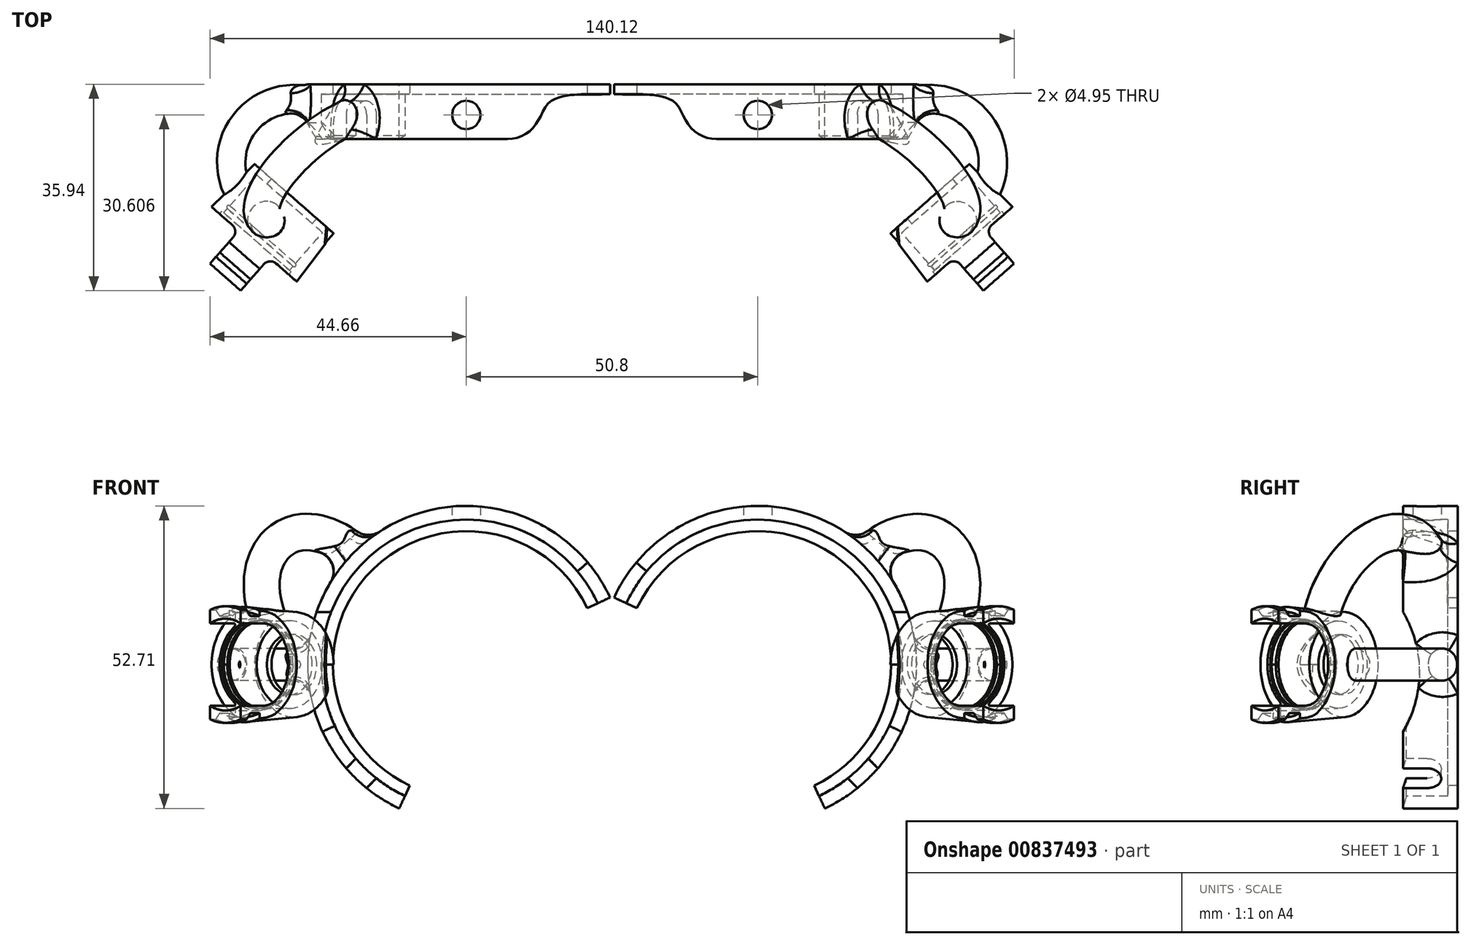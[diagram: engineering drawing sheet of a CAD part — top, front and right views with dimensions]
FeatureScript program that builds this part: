
annotation { "Feature Type Name" : "Feature", "Feature Type Description" : "" }
export const myFeature = defineFeature(function(context is Context, id is Id, definition is map)
    precondition{}
    {
        {
            var Q0;
            Q0=qCreatedBy(makeId("Front.planeOp"),FACE);
            var sketch = newSketch(context, id + "F0", { "sketchPlane" : qUnion([Q0])});
            skCircle(sketch, "E0", {"center": v(0, 0) * mm, "radius": 25.27 * mm, "construction": true});
            skCircle(sketch, "E1", {"center": v(0, 0) * mm, "radius": 23.24 * mm, "construction": true});
            skLineSegment(sketch, "E2", {"start": v(0, 0) * mm, "end": v(0, 25.27) * mm, "construction": true});
            skLineSegment(sketch, "E3", {"start": v(0, 0) * mm, "end": v(25.27, 0) * mm, "construction": true});
            skLineSegment(sketch, "E4", {"start": v(0, 0) * mm, "end": v(17.87, 17.87) * mm, "construction": true});
            skCircle(sketch, "E5", {"center": v(0, 0) * mm, "radius": 15.88 * mm, "construction": true});
            skPoint(sketch, "E6", {"position": v(17.87, 17.86) * mm});
            skLineSegment(sketch, "E7", {"start": v(0, 0) * mm, "end": v(17.55, -18.17) * mm, "construction": true});
            skPoint(sketch, "E8", {"position": v(17.88, -17.85) * mm});
            skSolve(sketch);
        }
        {
            var Q0;
            Q0=qCreatedBy(makeId("Right.planeOp"),FACE);
            var sketch = newSketch(context, id + "F1", { "sketchPlane" : qUnion([Q0])});
            skLineSegment(sketch, "E9.0", {"start": v(0, -25.27) * mm, "end": v(0, 25.27) * mm, "construction": true});
            skLineSegment(sketch, "E9.1", {"start": v(0, -23.24) * mm, "end": v(0, 23.24) * mm, "construction": true});
            skLineSegment(sketch, "E10", {"start": v(0, 23.24) * mm, "end": v(-1.73, 23.24) * mm});
            skLineSegment(sketch, "E11", {"start": v(-1.73, 23.24) * mm, "end": v(-1.73, 25.27) * mm});
            skLineSegment(sketch, "E12", {"start": v(-1.73, 25.27) * mm, "end": v(-9.53, 25.27) * mm});
            skLineSegment(sketch, "E13", {"start": v(0, 23.24) * mm, "end": v(0, 25.27) * mm});
            skLineSegment(sketch, "E14", {"start": v(-9.53, 25.27) * mm, "end": v(-9.53, 27.65) * mm});
            skLineSegment(sketch, "E15", {"start": v(-9.53, 27.65) * mm, "end": v(0, 27.65) * mm});
            skLineSegment(sketch, "E16", {"start": v(0, 27.65) * mm, "end": v(0, 25.27) * mm});
            skLineSegment(sketch, "E17", {"start": v(0, 0) * mm, "end": v(1.7, 0) * mm, "construction": true});
            skLineSegment(sketch, "E18.0", {"start": v(0, -15.88) * mm, "end": v(0, 15.88) * mm, "construction": true});
            skLineSegment(sketch, "E19", {"start": v(0, 15.88) * mm, "end": v(14.29, 15.88) * mm, "construction": true});
            skLineSegment(sketch, "E20", {"start": v(0, -15.88) * mm, "end": v(14.29, -15.88) * mm, "construction": true});
            skLineSegment(sketch, "E21", {"start": v(0, 27.65) * mm, "end": v(-14.29, 27.65) * mm, "construction": true});
            skLineSegment(sketch, "E22", {"start": v(0, -25.27) * mm, "end": v(-14.29, -25.27) * mm, "construction": true});
            skLineSegment(sketch, "E23", {"start": v(14.29, 15.88) * mm, "end": v(14.29, -15.88) * mm, "construction": true});
            skLineSegment(sketch, "E24", {"start": v(14.29, 0) * mm, "end": v(26.99, 0) * mm});
            skPoint(sketch, "E25", {"position": v(-5.16, 27.65) * mm});
            skSolve(sketch);
        }
        {
            var Q0;
            Q0=makeQuery(id+"F1.imprint","IMPRINT",FACE,{"disambiguationData":[TD([[makeQuery(id+"F1.imprint","IMPRINT",EDGE,{"derivedFrom":sQuery(id+"F1.wireOp",EDGE,"E10")}),-1.0]])]});
            var Q1;
            Q1=sQuery(id+"F1.wireOp",EDGE,"E17");
            revolve(context, id + "F2", {"surfaceOperationType" : NewSurfaceOperationType.NEW, "entities" : qUnion([Q0]), "axis" : qUnion([Q1]), "revolveType" : RevolveType.TWO_DIRECTIONS, "angle" : 115 * degree, "angleBack" : 310 * degree});
        }
        {
            var Q0;
            Q0=qCreatedBy(makeId("Top.planeOp"),FACE);
            var sketch = newSketch(context, id + "F3", { "sketchPlane" : qUnion([Q0])});
            skLineSegment(sketch, "E26.0", {"start": v(0, 14.29) * mm, "end": v(0, 26.99) * mm});
            skLineSegment(sketch, "E26.1.0", {"start": v(-21.18, -9.53) * mm, "end": v(27.65, -9.53) * mm});
            skLineSegment(sketch, "E26.1.1", {"start": v(25.06, -9.53) * mm, "end": v(25.06, 0) * mm});
            skLineSegment(sketch, "E26.1.2", {"start": v(27.65, 0) * mm, "end": v(-21.18, 0) * mm});
            skLineSegment(sketch, "E26.1.3", {"start": v(-21.18, 0) * mm, "end": v(-21.18, -9.53) * mm});
            skLineSegment(sketch, "E27", {"start": v(0, 14.29) * mm, "end": v(5.73, 19.31) * mm, "construction": true});
            skLineSegment(sketch, "E28", {"start": v(0, 14.29) * mm, "end": v(25.06, -14.29) * mm, "construction": true});
            skLineSegment(sketch, "E29", {"start": v(5.73, 19.31) * mm, "end": v(36.52, -15.8) * mm, "construction": true});
            skLineSegment(sketch, "E30", {"start": v(25.06, -9.53) * mm, "end": v(25.06, -19.05) * mm, "construction": true});
            skLineSegment(sketch, "E31.MirrorCS", {"start": v(-5.73, 9.26) * mm, "end": v(25.06, -25.85) * mm, "construction": true});
            skLineSegment(sketch, "E32.MirrorCS", {"start": v(0, 14.29) * mm, "end": v(-5.73, 9.26) * mm, "construction": true});
            skLineSegment(sketch, "E33", {"start": v(25.06, -19.05) * mm, "end": v(25.06, -25.85) * mm});
            skLineSegment(sketch, "E34", {"start": v(25.06, -25.85) * mm, "end": v(36.52, -15.8) * mm, "construction": true});
            skLineSegment(sketch, "E35", {"start": v(36.52, -15.8) * mm, "end": v(34.72, -17.37) * mm});
            skLineSegment(sketch, "E36", {"start": v(34.72, -17.37) * mm, "end": v(33.94, -16.47) * mm});
            skLineSegment(sketch, "E37", {"start": v(36.52, -15.8) * mm, "end": v(42.27, -22.36) * mm});
            skLineSegment(sketch, "E38", {"start": v(42.27, -22.36) * mm, "end": v(43.42, -21.36) * mm});
            skLineSegment(sketch, "E39", {"start": v(43.42, -21.36) * mm, "end": v(36.88, -13.9) * mm});
            skLineSegment(sketch, "E40", {"start": v(33.94, -16.47) * mm, "end": v(36.88, -13.9) * mm});
            skLineSegment(sketch, "E41", {"start": v(42.56, -22.11) * mm, "end": v(48, -28.32) * mm});
            skLineSegment(sketch, "E42", {"start": v(43.42, -21.36) * mm, "end": v(48.86, -27.56) * mm});
            skLineSegment(sketch, "E43", {"start": v(48, -28.32) * mm, "end": v(48.86, -27.56) * mm});
            skLineSegment(sketch, "E44", {"start": v(30.79, -20.82) * mm, "end": v(32.6, -22.88) * mm, "construction": true});
            skLineSegment(sketch, "E45", {"start": v(48.86, -27.56) * mm, "end": v(49.62, -26.9) * mm});
            skLineSegment(sketch, "E46", {"start": v(49.62, -26.9) * mm, "end": v(48.58, -25.7) * mm});
            skLineSegment(sketch, "E47", {"start": v(48.58, -25.7) * mm, "end": v(47.81, -26.37) * mm});
            skLineSegment(sketch, "E48", {"start": v(36.32, -15.96) * mm, "end": v(42.27, -22.36) * mm});
            skLineSegment(sketch, "E49", {"start": v(45.55, -23.8) * mm, "end": v(46.22, -23.2) * mm});
            skLineSegment(sketch, "E50", {"start": v(46.22, -23.2) * mm, "end": v(36.88, -13.9) * mm});
            skCircle(sketch, "E51", {"center": v(41.43, -21.4) * mm, "radius": 0.32 * mm});
            skSolve(sketch);
        }
        {
            var Q0;
            Q0=makeQuery(id+"F3.imprint","IMPRINT",FACE,{"disambiguationData":[TD([[makeQuery(id+"F3.imprint","IMPRINT",EDGE,{"derivedFrom":sQuery(id+"F3.wireOp",EDGE,"E35")}),-1.0]])]});
            var Q1;
            {var subQ2=sQuery(id+"F3.wireOp",EDGE,"E41");Q1=makeQuery(id+"F3.imprint","IMPRINT",FACE,{"disambiguationData":[TD([[makeQuery(id+"F3.imprint","IMPRINT",EDGE,{"derivedFrom":subQ2}),1.0]])]});}
            var Q2;
            {var subQ0=sQuery(id+"F3.wireOp",EDGE,"E45");Q2=makeQuery(id+"F3.imprint","IMPRINT",FACE,{"disambiguationData":[TD([[makeQuery(id+"F3.imprint","IMPRINT",EDGE,{"derivedFrom":subQ0}),1.0]])]});}
            var Q3;
            {var subQ0=sQuery(id+"F3.wireOp",EDGE,"ZS8Crhrf-CrOi-06I2-Trp5-8wOd5zCYoBhE");Q3=makeQuery(id+"F3.imprint","IMPRINT",FACE,{"disambiguationData":[TD([[makeQuery(id+"F3.imprint","IMPRINT",EDGE,{"derivedFrom":subQ0}),-1.0]])]});}
            var Q4;
            {var subQ0=sQuery(id+"F3.wireOp",EDGE,"E39");Q4=makeQuery(id+"F3.imprint","IMPRINT",FACE,{"disambiguationData":[TD([[makeQuery(id+"F3.imprint","IMPRINT",EDGE,{"derivedFrom":subQ0}),-1.0]])]});}
            var Q5;
            {var subQ0=sQuery(id+"F3.wireOp",EDGE,"E51");var subQ1=sQuery(id+"F3.wireOp",EDGE,"E37");var subQ2=makeQuery(id+"F3.imprint","INTERSECT",VERTEX,{"disambiguationData":[OD(0.0)],"derivedFrom":[subQ1,subQ0]});Q5=makeQuery(id+"F3.imprint","IMPRINT",FACE,{"disambiguationData":[TD([[makeQuery(id+"F3.imprint","IMPRINT",EDGE,{"disambiguationData":[TD([[subQ2,-1.0]])],"derivedFrom":subQ1}),1.0]])]});}
            var Q6;
            Q6=sQuery(id+"F3.wireOp",EDGE,"E44");
            var Q7;
            Q7=sQuery(id+"F3.wireOp",EDGE,"E44");
            revolve(context, id + "F4", {"operationType" : NewBodyOperationType.ADD, "surfaceOperationType" : NewSurfaceOperationType.NEW, "entities" : qUnion([Q0, Q1, Q2, Q3, Q4, Q5]), "surfaceEntities" : qUnion([Q6]), "axis" : qUnion([Q7]), "revolveType" : RevolveType.FULL});
        }
        {
            var Q0;
            Q0=qCreatedBy(makeId("Right.planeOp"),FACE);
            var sketch = newSketch(context, id + "F5", { "sketchPlane" : qUnion([Q0])});
            skEllipse(sketch, "E52.0", {"center": v(-19.93, 0) * mm, "majorRadius": 8.76 * mm, "minorRadius": 5.18 * mm, "majorAxis": v(0, -1), "construction": true});
            skLineSegment(sketch, "E52.1.0", {"start": v(-9.53, 27.65) * mm, "end": v(-9.53, -11.68) * mm, "construction": true});
            skLineSegment(sketch, "E52.1.1", {"start": v(-9.53, -11.68) * mm, "end": v(0, -11.68) * mm});
            skLineSegment(sketch, "E52.1.2", {"start": v(0, -11.68) * mm, "end": v(0, 27.65) * mm});
            skLineSegment(sketch, "E52.1.3", {"start": v(0, 17.77) * mm, "end": v(-9.53, 17.77) * mm, "construction": true});
            skLineSegment(sketch, "E53", {"start": v(-19.93, 0) * mm, "end": v(-9.53, 0) * mm, "construction": true});
            skLineSegment(sketch, "E54", {"start": v(-19.93, 9.14) * mm, "end": v(-9.53, 9.14) * mm, "construction": true});
            skLineSegment(sketch, "E55", {"start": v(-19.93, -9.14) * mm, "end": v(-9.53, -9.14) * mm, "construction": true});
            skLineSegment(sketch, "E56", {"start": v(-9.53, 9.14) * mm, "end": v(-9.53, -9.14) * mm});
            skArc(sketch, "E57", {"start": v(-9.53, -11.68) * mm, "mid": v(-6.65, -1.27) * mm, "end": v(-9.53, 9.14) * mm});
            skLineSegment(sketch, "E58", {"start": v(-9.53, -9.14) * mm, "end": v(-9.53, -11.68) * mm});
            skSolve(sketch);
        }
        {
            var Q0;
            Q0=makeQuery(id+"F5.imprint","IMPRINT",FACE,{"disambiguationData":[TD([[makeQuery(id+"F5.imprint","IMPRINT",EDGE,{"derivedFrom":sQuery(id+"F5.wireOp",EDGE,"GxEW9ax0-zjAY-ybk5-duMN-0JDvZg63hfbD")}),1.0]])]});
            var Q1;
            Q1=makeQuery(id+"F5.imprint","IMPRINT",FACE,{"disambiguationData":[TD([[makeQuery(id+"F5.imprint","IMPRINT",EDGE,{"derivedFrom":sQuery(id+"F5.wireOp",EDGE,"E56")}),1.0]])]});
            extrude(context, id + "F6", {"entities" : qUnion([Q0, Q1]), "operationType" : NewBodyOperationType.REMOVE, "depth" : 50.57 * mm, "offsetDistance" : 25.4 * mm});
        }
        {
            var Q0;
            Q0=qCreatedBy(makeId("Top.planeOp"),FACE);
            var sketch = newSketch(context, id + "F7", { "sketchPlane" : qUnion([Q0])});
            skLineSegment(sketch, "E59.1.0", {"start": v(-21.18, -9.53) * mm, "end": v(26.26, -9.53) * mm, "construction": true});
            skLineSegment(sketch, "E59.1.2", {"start": v(25.06, -11.07) * mm, "end": v(25.06, 0) * mm, "construction": true});
            skLineSegment(sketch, "E59.1.3", {"start": v(27.65, 0) * mm, "end": v(-21.18, 0) * mm, "construction": true});
            skLineSegment(sketch, "E59.1.4", {"start": v(-21.18, 0) * mm, "end": v(-21.18, -9.53) * mm});
            skLineSegment(sketch, "E60.0", {"start": v(26.06, -23.38) * mm, "end": v(33.94, -16.47) * mm, "construction": true});
            skLineSegment(sketch, "E60.1", {"start": v(23.13, -25.95) * mm, "end": v(36.88, -13.9) * mm, "construction": true});
            skLineSegment(sketch, "E60.3", {"start": v(30.81, -32.4) * mm, "end": v(42.27, -22.36) * mm, "construction": true});
            skLineSegment(sketch, "E60.4", {"start": v(25.06, -25.85) * mm, "end": v(36.52, -15.8) * mm, "construction": true});
            skLineSegment(sketch, "E61", {"start": v(36.52, -15.8) * mm, "end": v(42.27, -22.36) * mm, "construction": true});
            skPoint(sketch, "E62", {"position": v(25.06, -3.81) * mm});
            skPoint(sketch, "E62.positionSnap0", {"position": v(27.71, -3.81) * mm});
            skArc(sketch, "E63", {"start": v(39.4, -19.08) * mm, "mid": v(37.93, -6.1) * mm, "end": v(25.06, -3.81) * mm});
            skSolve(sketch);
        }
        {
            var Q0;
            Q0=sQuery(id+"F7.wireOp",EDGE,"E59.1.2");
            cPlane(context, id + "F8", {"entities" : qUnion([Q0]), "cplaneType" : CPlaneType.LINE_ANGLE, "offset" : 25.4 * mm, "angle" : 90 * degree, "width" : 152.4 * mm, "height" : 152.4 * mm});
        }
        {
            var Q0;
            Q0=qCreatedBy(id+"F8.planeOp",FACE);
            var sketch = newSketch(context, id + "F9", { "sketchPlane" : qUnion([Q0])});
            skPoint(sketch, "E64.0", {"position": v(-3.81, 0) * mm});
            skCircle(sketch, "E65", {"center": v(-3.81, 0) * mm, "radius": 2.8 * mm});
            skSolve(sketch);
        }
        {
            var Q0;
            Q0=qSketchRegion(id+"F9",true);
            var Q1;
            Q1=sQuery(id+"F7.wireOp",EDGE,"E63");
            sweep(context, id + "F10", {"operationType" : NewBodyOperationType.ADD, "profiles" : qUnion([Q0]), "path" : qUnion([Q1])});
        }
        {
            var Q0;
            Q0=makeQuery(id+"F2.opRevolve","SWEPT_FACE",FACE,{"disambiguationData":[OSD([sQuery(id+"F1.wireOp",EDGE,"E11")])]});
            var sketch = newSketch(context, id + "F11", { "sketchPlane" : qUnion([Q0])});
            skPoint(sketch, "E66.0", {"position": v(17.87, 17.86) * mm});
            skSolve(sketch);
        }
        {
            var Q0;
            Q0=sQuery(id+"F11.wireOp",VERTEX,"E66.0");
            var Q1;
            Q1=sQuery(id+"F0.wireOp",VERTEX,"E4.end");
            var Q2;
            Q2=sQuery(id+"F0.wireOp",VERTEX,"E6");
            cPlane(context, id + "F12", {"entities" : qUnion([Q0, Q1, Q2]), "cplaneType" : CPlaneType.THREE_POINT, "offset" : 25.4 * mm, "width" : 152.4 * mm, "height" : 152.4 * mm});
        }
        {
            var Q0;
            Q0=makeQuery(id+"F4.opRevolve","SWEPT_FACE",FACE,{"disambiguationData":[OSD([sQuery(id+"F3.wireOp",EDGE,"E35")])]});
            var sketch = newSketch(context, id + "F13", { "sketchPlane" : qUnion([Q0])});
            skPoint(sketch, "E67.0", {"position": v(13.44, 17.86) * mm});
            skLineSegment(sketch, "E68", {"start": v(13.03, 18) * mm, "end": v(8.4, 5.09) * mm, "construction": true});
            skSolve(sketch);
        }
        {
            var Q0;
            Q0=qCreatedBy(id+"F12.planeOp",FACE);
            var sketch = newSketch(context, id + "F14", { "sketchPlane" : qUnion([Q0])});
            skLineSegment(sketch, "E69", {"start": v(0, 0) * mm, "end": v(-9.53, 0) * mm, "construction": true});
            skLineSegment(sketch, "E70.0", {"start": v(-9.53, -5.93) * mm, "end": v(-9.53, 27.65) * mm, "construction": true});
            skCircle(sketch, "E71", {"center": v(-4.76, 0) * mm, "radius": 3.18 * mm});
            skSolve(sketch);
        }
        {
            var Q0;
            Q0=sQuery(id+"F14.wireOp",EDGE,"E69");
            cPoint(context, id + "F15", {"entities" : qUnion([Q0]), "parameter" : 0.5});
        }
        {
            var Q0;
            Q0=sQuery(id+"F13.wireOp",VERTEX,"E68.end");
            var Q1;
            Q1=sQuery(id+"F13.wireOp",VERTEX,"E67.0");
            var Q2;
            Q2=qCreatedBy(id+"F15",VERTEX);
            cPlane(context, id + "F16", {"entities" : qUnion([Q0, Q1, Q2]), "cplaneType" : CPlaneType.THREE_POINT, "offset" : 25.4 * mm, "width" : 152.4 * mm, "height" : 152.4 * mm});
        }
        {
            var Q0;
            Q0=qCreatedBy(id+"F16.planeOp",FACE);
            var sketch = newSketch(context, id + "F17", { "sketchPlane" : qUnion([Q0])});
            skEllipse(sketch, "E72.0", {"center": v(-35.76, -9.46) * mm, "majorRadius": 7.47 * mm, "minorRadius": 0.91 * mm, "majorAxis": v(0.35, -0.94), "construction": true});
            skEllipse(sketch, "E72.1", {"center": v(-43.87, -12.44) * mm, "majorRadius": 7.47 * mm, "minorRadius": 0.91 * mm, "majorAxis": v(0.35, -0.94), "construction": true});
            skLineSegment(sketch, "E73", {"start": v(-38.39, -2.3) * mm, "end": v(-46.5, -5.3) * mm, "construction": true});
            skPoint(sketch, "E74.0", {"position": v(-21.71, 13.75) * mm});
            skArc(sketch, "E75", {"start": v(-21.71, 13.75) * mm, "mid": v(-38.99, 13.14) * mm, "end": v(-42.45, -3.8) * mm});
            skSolve(sketch);
        }
        {
            var Q0;
            Q0=qSketchRegion(id+"F14",true);
            var Q1;
            Q1=sQuery(id+"F17.wireOp",EDGE,"E75");
            sweep(context, id + "F18", {"operationType" : NewBodyOperationType.ADD, "profiles" : qUnion([Q0]), "path" : qUnion([Q1])});
        }
        {
            var Q0;
            Q0=qCreatedBy(makeId("Top.planeOp"),FACE);
            var sketch = newSketch(context, id + "F19", { "sketchPlane" : qUnion([Q0])});
            skLineSegment(sketch, "E76.0", {"start": v(30.53, -32.66) * mm, "end": v(42.56, -22.11) * mm, "construction": true});
            skLineSegment(sketch, "E77.0", {"start": v(22.9, -1.73) * mm, "end": v(22.9, -1.73) * mm});
            skLineSegment(sketch, "E78.0", {"start": v(-21.18, -9.53) * mm, "end": v(-21.18, 0) * mm, "construction": true});
            skLineSegment(sketch, "E78.1", {"start": v(-7.2, -9.53) * mm, "end": v(-21.18, -9.53) * mm, "construction": true});
            skLineSegment(sketch, "E79", {"start": v(-21.18, -1.73) * mm, "end": v(-25.57, -1.73) * mm});
            skLineSegment(sketch, "E80", {"start": v(-25.57, -1.73) * mm, "end": v(-25.57, -14.68) * mm});
            skLineSegment(sketch, "E81", {"start": v(-25.57, -14.68) * mm, "end": v(-7.2, -14.68) * mm});
            skLineSegment(sketch, "E82", {"start": v(-7.2, -14.68) * mm, "end": v(-7.2, -9.53) * mm});
            skFitSpline(sketch, "E83", {"points": [v(42.56, -22.11) * mm, v(35.64, -31.83) * mm, v(34.35, -40.3) * mm], "startDerivative": vector(-16.46, -14.44) * mm, "endDerivative": vector(-39.72, -35.09) * mm, "construction": true});
            skLineSegment(sketch, "E84", {"start": v(42.56, -22.11) * mm, "end": v(44.84, -20.17) * mm});
            skLineSegment(sketch, "E85", {"start": v(44.84, -20.17) * mm, "end": v(52.02, -28.58) * mm});
            skLineSegment(sketch, "E86", {"start": v(52.02, -28.58) * mm, "end": v(36.12, -42.17) * mm});
            skLineSegment(sketch, "E87", {"start": v(36.12, -42.17) * mm, "end": v(34.35, -40.3) * mm});
            skFitSpline(sketch, "E88", {"points": [v(-21.18, -1.73) * mm, v(-12.95, -5.57) * mm, v(-7.2, -9.53) * mm], "startDerivative": vector(39.3, 0) * mm, "endDerivative": vector(20.69, 0) * mm});
            skSolve(sketch);
        }
        {
            var Q0;
            Q0=qSketchRegion(id+"F19",true);
            extrude(context, id + "F20", {"entities" : qUnion([Q0]), "operationType" : NewBodyOperationType.REMOVE, "endBound" : BoundingType.SYMMETRIC, "oppositeDirection" : true, "depth" : 82.8 * mm, "offsetDistance" : 25.4 * mm});
        }
        {
            var Q0;
            Q0=qCreatedBy(makeId("Top.planeOp"),FACE);
            var sketch = newSketch(context, id + "F21", { "sketchPlane" : qUnion([Q0])});
            skCircle(sketch, "E89", {"center": v(0, -5.33) * mm, "radius": 2.48 * mm});
            skSolve(sketch);
        }
        {
            var Q0;
            Q0=makeQuery(id+"F21.imprint","IMPRINT",FACE,{"disambiguationData":[TD([[makeQuery(id+"F21.imprint","IMPRINT",EDGE,{"derivedFrom":sQuery(id+"F21.wireOp",EDGE,"E89")}),1.0]])]});
            extrude(context, id + "F22", {"entities" : qUnion([Q0]), "operationType" : NewBodyOperationType.REMOVE, "depth" : 31.5 * mm, "offsetDistance" : 25.4 * mm});
        }
        {
            var Q0;
            Q0=makeQuery(id+"F10.opSweep","CAP_EDGE",EDGE,{"disambiguationData":[OSD([sQuery(id+"F7.wireOp",VERTEX,"E63.start"),sQuery(id+"F9.wireOp",EDGE,"E65")])],"isStart":false});
            chamfer(context, id + "F23", {"entities" : qUnion([Q0]), "width" : 1.52 * mm, "tangentPropagation" : true});
        }
        {
            var Q0;
            Q0=makeQuery(id+"F2.opRevolve","SWEPT_FACE",FACE,{"disambiguationData":[OSD([sQuery(id+"F1.wireOp",EDGE,"E11")])]});
            var sketch = newSketch(context, id + "F24", { "sketchPlane" : qUnion([Q0])});
            skArc(sketch, "E90.0", {"start": v(22.9, -10.68) * mm, "mid": v(24.44, -6.4) * mm, "end": v(25.2, -1.92) * mm});
            skCircle(sketch, "E91", {"center": v(0, 0) * mm, "radius": 24.48 * mm});
            skArc(sketch, "E92.0", {"start": v(25.2, 1.92) * mm, "mid": v(-25.27, 0) * mm, "end": v(25.2, -1.92) * mm});
            skPoint(sketch, "E93.0", {"position": v(17.87, 17.86) * mm});
            skCircle(sketch, "E94", {"center": v(0, 0) * mm, "radius": 25.27 * mm});
            skSolve(sketch);
        }
        {
            var Q0;
            {var subQ1=sQuery(id+"F1.wireOp",EDGE,"E11");var subQ6=makeQuery(id+"F2.opRevolve","SWEPT_EDGE",EDGE,{"disambiguationData":[OSD([sQuery(id+"F1.wireOp",EDGE,"E10"),subQ1])]});Q0=makeQuery(id+"F24.imprint","IMPRINT",FACE,{"disambiguationData":[TD([[makeQuery(id+"F24.imprint","IMPRINT",EDGE,{"derivedFrom":subQ6}),1.0]])]});}
            var Q1;
            {var subQ1=sQuery(id+"F1.wireOp",EDGE,"E11");var subQ6=makeQuery(id+"F2.opRevolve","SWEPT_EDGE",EDGE,{"disambiguationData":[OSD([sQuery(id+"F1.wireOp",EDGE,"E10"),subQ1])]});Q1=makeQuery(id+"F24.imprint","IMPRINT",FACE,{"disambiguationData":[TD([[makeQuery(id+"F24.imprint","IMPRINT",EDGE,{"derivedFrom":subQ6}),-1.0]])]});}
            extrude(context, id + "F25", {"entities" : qUnion([Q0, Q1]), "operationType" : NewBodyOperationType.REMOVE, "depth" : 43.43 * mm, "offsetDistance" : 25.4 * mm});
        }
        {
            var Q0;
            Q0=makeQuery(id+"F2.opRevolve","CAP_FACE",FACE,{"disambiguationData":[OSD([sQuery(id+"F1.wireOp",EDGE,"E10"),sQuery(id+"F1.wireOp",EDGE,"E11"),sQuery(id+"F1.wireOp",EDGE,"E12"),sQuery(id+"F1.wireOp",EDGE,"E13"),sQuery(id+"F1.wireOp",EDGE,"E14"),sQuery(id+"F1.wireOp",EDGE,"E15"),sQuery(id+"F1.wireOp",EDGE,"E16")])],"isStart":false});
            var Q1;
            Q1=sQuery(id+"F1.wireOp",EDGE,"E24");
            revolve(context, id + "F26", {"operationType" : NewBodyOperationType.ADD, "surfaceOperationType" : NewSurfaceOperationType.NEW, "entities" : qUnion([Q0]), "axis" : qUnion([Q1]), "revolveType" : RevolveType.ONE_DIRECTION, "angle" : 40 * degree});
        }
        {
            var Q0;
            {var subQ0=sQuery(id+"F1.wireOp",EDGE,"E11");Q0=makeQuery(id+"F26.boolean.opBoolean","MERGE",FACE,{"derivedFrom":[makeQuery(id+"F2.opRevolve","SWEPT_FACE",FACE,{"disambiguationData":[OSD([subQ0])]}),makeQuery(id+"F26.opRevolve","SWEPT_FACE",FACE,{"disambiguationData":[OSD([subQ0])]})]});}
            var sketch = newSketch(context, id + "F27", { "sketchPlane" : qUnion([Q0])});
            skPoint(sketch, "E95.0", {"position": v(17.55, -18.17) * mm});
            skSolve(sketch);
        }
        {
            var Q0;
            Q0=sQuery(id+"F0.wireOp",VERTEX,"E7.end");
            var Q1;
            Q1=sQuery(id+"F0.wireOp",VERTEX,"E8");
            var Q2;
            Q2=sQuery(id+"F27.wireOp",VERTEX,"E95.0");
            cPlane(context, id + "F28", {"entities" : qUnion([Q0, Q1, Q2]), "cplaneType" : CPlaneType.THREE_POINT, "offset" : 25.4 * mm, "width" : 152.4 * mm, "height" : 152.4 * mm});
        }
        {
            var Q0;
            Q0=qCreatedBy(id+"F28.planeOp",FACE);
            var sketch = newSketch(context, id + "F29", { "sketchPlane" : qUnion([Q0])});
            skCircle(sketch, "E96", {"center": v(-0.23, -5.33) * mm, "radius": 2.48 * mm});
            skPoint(sketch, "E97.0", {"position": v(-0.23, 0) * mm});
            skLineSegment(sketch, "E98.0", {"start": v(-9.24, -9.52) * mm, "end": v(9.67, -9.52) * mm});
            skLineSegment(sketch, "E99", {"start": v(2.25, -5.33) * mm, "end": v(2.25, -9.52) * mm});
            skLineSegment(sketch, "E100", {"start": v(-2.7, -5.33) * mm, "end": v(-2.7, -9.52) * mm});
            skSolve(sketch);
        }
        {
            var Q0;
            Q0 = qSketchRegion(id + "F29", true);
            extrude(context, id + "F30", {"entities" : qUnion([Q0]), "operationType" : NewBodyOperationType.REMOVE, "endBound" : BoundingType.SYMMETRIC, "oppositeDirection" : true, "depth" : 25.4 * mm, "offsetDistance" : 25.4 * mm});
        }
        {
            var Q0;
            Q0=makeQuery(id+"F2.opRevolve","CAP_FACE",FACE,{"disambiguationData":[OSD([sQuery(id+"F1.wireOp",EDGE,"E10"),sQuery(id+"F1.wireOp",EDGE,"E11"),sQuery(id+"F1.wireOp",EDGE,"E12"),sQuery(id+"F1.wireOp",EDGE,"E13"),sQuery(id+"F1.wireOp",EDGE,"E14"),sQuery(id+"F1.wireOp",EDGE,"E15"),sQuery(id+"F1.wireOp",EDGE,"E16")])],"isStart":true});
            var Q1;
            Q1=sQuery(id+"F1.wireOp",EDGE,"E24");
            revolve(context, id + "F31", {"operationType" : NewBodyOperationType.ADD, "surfaceOperationType" : NewSurfaceOperationType.NEW, "entities" : qUnion([Q0]), "axis" : qUnion([Q1]), "revolveType" : RevolveType.ONE_DIRECTION, "oppositeDirection" : true, "angle" : 15 * degree});
        }
        {
            var Q0;
            Q0=makeQuery(id+"F25.boolean.opBoolean","COPY",FACE,{"derivedFrom":makeQuery(id+"F25.opExtrude","SWEPT_FACE",FACE,{"disambiguationData":[OSD([sQuery(id+"F24.wireOp",EDGE,"E91")])]})});
            fillet(context, id + "F32", {"entities" : qUnion([Q0]), "radius" : 1.02 * mm, "tangentPropagation" : true, "allowEdgeOverflow" : false});
        }
        {
            var Q0;
            Q0 = qSketchRegion(id + "F24", true);
            var Q1;
            {var subQ0=sQuery(id+"F1.wireOp",EDGE,"E11");Q1=makeQuery(id+"F31.boolean.opBoolean","MERGE",FACE,{"derivedFrom":[makeQuery(id+"F26.boolean.opBoolean","MERGE",FACE,{"derivedFrom":[makeQuery(id+"F2.opRevolve","SWEPT_FACE",FACE,{"disambiguationData":[OSD([subQ0])]}),makeQuery(id+"F26.opRevolve","SWEPT_FACE",FACE,{"disambiguationData":[OSD([subQ0])]})]}),makeQuery(id+"F31.opRevolve","SWEPT_FACE",FACE,{"disambiguationData":[OSD([subQ0])]})]});}
            extrude(context, id + "F33", {"entities" : qUnion([Q0, Q1]), "operationType" : NewBodyOperationType.REMOVE, "depth" : 7.87 * mm, "offsetDistance" : 25.4 * mm});
        }
        {
            var Q0;
            Q0=makeQuery(id+"F4.opRevolve","SWEPT_EDGE",EDGE,{"disambiguationData":[OSD([sQuery(id+"F3.wireOp",EDGE,"E42"),sQuery(id+"F3.wireOp",EDGE,"E47")])]});
            chamfer(context, id + "F34", {"entities" : qUnion([Q0]), "width" : 1.02 * mm, "tangentPropagation" : true});
        }
        {
            var Q0;
            Q0=qCreatedBy(makeId("Right.planeOp"),FACE);
            cPlane(context, id + "F35", {"entities" : qUnion([Q0]), "cplaneType" : CPlaneType.OFFSET, "offset" : 25.4 * mm, "oppositeDirection" : true, "width" : 152.4 * mm, "height" : 152.4 * mm});
        }
        {
            var Q0;
            Q0=makeQuery(id+"F4.opRevolve","SWEPT_FACE",FACE,{"disambiguationData":[OSD([sQuery(id+"F3.wireOp",EDGE,"E43"),sQuery(id+"F3.wireOp",EDGE,"E45"),sQuery(id+"F3.wireOp",EDGE,"ZS8Crhrf-CrOi-06I2-Trp5-8wOd5zCYoBhE")])]});
            var sketch = newSketch(context, id + "F36", { "sketchPlane" : qUnion([Q0])});
            skCircle(sketch, "E101.0", {"center": v(9.42, 0) * mm, "radius": 8 * mm, "construction": true});
            skLineSegment(sketch, "E102.bottom", {"start": v(21.87, -12.7) * mm, "end": v(12.98, -12.7) * mm});
            skLineSegment(sketch, "E102.top", {"start": v(21.87, 12.7) * mm, "end": v(12.98, 12.7) * mm});
            skLineSegment(sketch, "E102.left", {"start": v(21.87, -12.7) * mm, "end": v(21.87, 12.7) * mm});
            skLineSegment(sketch, "E102.right", {"start": v(12.98, -12.7) * mm, "end": v(12.98, 12.7) * mm});
            skPoint(sketch, "E102.middle", {"position": v(17.42, 0) * mm});
            skLineSegment(sketch, "E103", {"start": v(9.42, 0) * mm, "end": v(9.42, -1) * mm});
            skLineSegment(sketch, "E104.MirrorCS", {"start": v(-3.03, -12.7) * mm, "end": v(-3.03, 12.7) * mm});
            skLineSegment(sketch, "E105.MirrorCS", {"start": v(5.86, -12.7) * mm, "end": v(5.86, 12.7) * mm});
            skLineSegment(sketch, "E106.MirrorCS", {"start": v(-3.03, 12.7) * mm, "end": v(5.86, 12.7) * mm});
            skPoint(sketch, "E107.MirrorP", {"position": v(1.42, 0) * mm});
            skLineSegment(sketch, "E108.MirrorCS", {"start": v(-3.03, -12.7) * mm, "end": v(5.86, -12.7) * mm});
            skSolve(sketch);
        }
        {
            var Q0;
            Q0 = qSketchRegion(id + "F36", true);
            extrude(context, id + "F37", {"entities" : qUnion([Q0]), "operationType" : NewBodyOperationType.REMOVE, "oppositeDirection" : true, "depth" : 7.62 * mm, "offsetDistance" : 25.4 * mm});
        }
        {
            var Q0;
            Q0=makeQuery(id+"F18.boolean.opBoolean","INTERSECT",EDGE,{"derivedFrom":[makeQuery(id+"F2.opRevolve","SWEPT_FACE",FACE,{"disambiguationData":[OSD([sQuery(id+"F1.wireOp",EDGE,"E15")])]}),makeQuery(id+"F18.opSweep","SWEPT_FACE",FACE,{"disambiguationData":[OSD([sQuery(id+"F14.wireOp",EDGE,"E71"),sQuery(id+"F17.wireOp",EDGE,"E75")])]})]});
            var Q1;
            Q1=makeQuery(id+"F10.boolean.opBoolean","INTERSECT",EDGE,{"derivedFrom":[makeQuery(id+"F2.opRevolve","SWEPT_FACE",FACE,{"disambiguationData":[OSD([sQuery(id+"F1.wireOp",EDGE,"E15")])]}),makeQuery(id+"F10.opSweep","SWEPT_FACE",FACE,{"disambiguationData":[OSD([sQuery(id+"F7.wireOp",EDGE,"E63"),sQuery(id+"F9.wireOp",EDGE,"E65")])]})]});
            var Q2;
            Q2=makeQuery(id+"F18.boolean.opBoolean","INTERSECT",EDGE,{"derivedFrom":[makeQuery(id+"F4.opRevolve","SWEPT_FACE",FACE,{"disambiguationData":[OSD([sQuery(id+"F3.wireOp",EDGE,"E39"),sQuery(id+"F3.wireOp",EDGE,"E42")])]}),makeQuery(id+"F18.opSweep","SWEPT_FACE",FACE,{"disambiguationData":[OSD([sQuery(id+"F14.wireOp",EDGE,"E71"),sQuery(id+"F17.wireOp",EDGE,"E75")])]})]});
            var Q3;
            Q3=makeQuery(id+"F10.boolean.opBoolean","INTERSECT",EDGE,{"derivedFrom":[makeQuery(id+"F4.opRevolve","SWEPT_FACE",FACE,{"disambiguationData":[OSD([sQuery(id+"F3.wireOp",EDGE,"E39"),sQuery(id+"F3.wireOp",EDGE,"E42")])]}),makeQuery(id+"F10.opSweep","SWEPT_FACE",FACE,{"disambiguationData":[OSD([sQuery(id+"F7.wireOp",EDGE,"E63"),sQuery(id+"F9.wireOp",EDGE,"E65")])]})]});
            fillet(context, id + "F38", {"entities" : qUnion([Q0, Q1, Q2, Q3]), "radius" : 3.56 * mm, "tangentPropagation" : true, "allowEdgeOverflow" : false});
        }
        {
            var Q0;
            Q0=makeQuery(id+"F37.boolean.opBoolean","COPY",EDGE,{"disambiguationData":[OD(1.0)],"derivedFrom":makeQuery(id+"F37.opExtrude","CAP_EDGE",EDGE,{"disambiguationData":[OSD([sQuery(id+"F36.wireOp",EDGE,"E102.right")])],"isStart":false})});
            var Q1;
            Q1=makeQuery(id+"F37.boolean.opBoolean","COPY",EDGE,{"disambiguationData":[OD(0.0)],"derivedFrom":makeQuery(id+"F37.opExtrude","CAP_EDGE",EDGE,{"disambiguationData":[OSD([sQuery(id+"F36.wireOp",EDGE,"E102.right")])],"isStart":false})});
            var Q2;
            Q2=makeQuery(id+"F37.boolean.opBoolean","COPY",EDGE,{"disambiguationData":[OD(0.0)],"derivedFrom":makeQuery(id+"F37.opExtrude","CAP_EDGE",EDGE,{"disambiguationData":[OSD([sQuery(id+"F36.wireOp",EDGE,"E105.MirrorCS")])],"isStart":false})});
            var Q3;
            Q3=makeQuery(id+"F37.boolean.opBoolean","COPY",EDGE,{"disambiguationData":[OD(1.0)],"derivedFrom":makeQuery(id+"F37.opExtrude","CAP_EDGE",EDGE,{"disambiguationData":[OSD([sQuery(id+"F36.wireOp",EDGE,"E105.MirrorCS")])],"isStart":false})});
            fillet(context, id + "F39", {"entities" : qUnion([Q0, Q1, Q2, Q3]), "radius" : 1.52 * mm, "tangentPropagation" : true, "allowEdgeOverflow" : false});
        }
        {
            var Q0;
            {var subQ0=sQuery(id+"F3.wireOp",EDGE,"E51");var subQ1=sQuery(id+"F3.wireOp",EDGE,"E48");var subQ2=makeQuery(id+"F3.imprint","INTERSECT",VERTEX,{"disambiguationData":[OD(0.0)],"derivedFrom":[subQ1,subQ0]});Q0=makeQuery(id+"F3.imprint","IMPRINT",FACE,{"disambiguationData":[TD([[makeQuery(id+"F3.imprint","IMPRINT",EDGE,{"disambiguationData":[TD([[subQ2,-1.0]])],"derivedFrom":subQ1}),-1.0]])]});}
            var Q1;
            {var subQ0=sQuery(id+"F3.wireOp",EDGE,"E51");var subQ1=sQuery(id+"F3.wireOp",EDGE,"E37");var subQ2=makeQuery(id+"F3.imprint","INTERSECT",VERTEX,{"disambiguationData":[OD(0.0)],"derivedFrom":[subQ1,subQ0]});Q1=makeQuery(id+"F3.imprint","IMPRINT",FACE,{"disambiguationData":[TD([[makeQuery(id+"F3.imprint","IMPRINT",EDGE,{"disambiguationData":[TD([[subQ2,-1.0]])],"derivedFrom":subQ1}),1.0]])]});}
            var Q2;
            {var subQ0=sQuery(id+"F3.wireOp",EDGE,"E51");var subQ1=sQuery(id+"F3.wireOp",EDGE,"E37");var subQ2=makeQuery(id+"F3.imprint","INTERSECT",VERTEX,{"disambiguationData":[OD(0.0)],"derivedFrom":[subQ1,subQ0]});Q2=makeQuery(id+"F3.imprint","IMPRINT",FACE,{"disambiguationData":[TD([[makeQuery(id+"F3.imprint","IMPRINT",EDGE,{"disambiguationData":[TD([[subQ2,-1.0]])],"derivedFrom":subQ1}),-1.0]])]});}
            var Q3;
            Q3=sQuery(id+"F3.wireOp",EDGE,"E44");
            revolve(context, id + "F40", {"operationType" : NewBodyOperationType.ADD, "surfaceOperationType" : NewSurfaceOperationType.NEW, "entities" : qUnion([Q0, Q1, Q2]), "axis" : qUnion([Q3]), "revolveType" : RevolveType.ONE_DIRECTION, "angle" : 180 * degree});
        }
        {
            var Q0;
            Q0=makeQuery(id+"F2.opRevolve","SWEPT_BODY",BODY,{"disambiguationData":[OSD([sQuery(id+"F1.wireOp",EDGE,"E10"),sQuery(id+"F1.wireOp",EDGE,"E11"),sQuery(id+"F1.wireOp",EDGE,"E12"),sQuery(id+"F1.wireOp",EDGE,"E13"),sQuery(id+"F1.wireOp",EDGE,"E14"),sQuery(id+"F1.wireOp",EDGE,"E15"),sQuery(id+"F1.wireOp",EDGE,"E16")])]});
            var Q1;
            Q1=qCreatedBy(id+"F35.planeOp",FACE);
            mirror(context, id + "F41", {"entities" : qUnion([Q0]), "mirrorPlane" : qUnion([Q1])});
        }
    });
